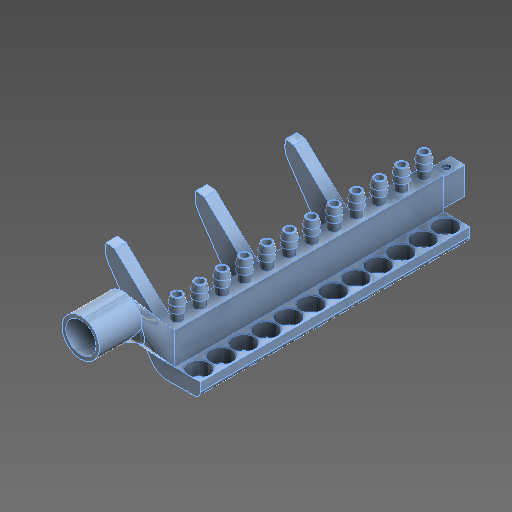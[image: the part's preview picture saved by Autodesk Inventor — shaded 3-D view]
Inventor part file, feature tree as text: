
AUTODESK INVENTOR PART (.ipt)
format: ipt  version: 2020 (Build 240168000, 168)  size: 707,584 bytes
history: native  units: in
note: dims shown in document units (in); Inventor stores cm internally (conversion verified against a paired STEP export)
features: other x13, extrude x7, pattern_linear x4, fillet x4, loft x2, projected_geometry x1, sketch x1
ambient origin geometry x8: Origin, YZ Plane, XZ Plane, XY Plane, X Axis, Y Axis, Z Axis, Center Point
bodies: Body1 (feature_tree)
feature tree (32):
  other  "CrossSection1"
  other  "Silicone Fitting Plane"
  other  "Cap Plane"
  other  "Base Sketch"
  extrude  "Base"  Depth=0.315in
  extrude  "Lip"  Depth=0.315in
  extrude  "Tube Socket"  Depth=0.315in
  pattern_linear  "Tube Socket Repetition"  Spacing1=0.0197in  [1 undecoded]
  other  "Silicone Fitting"
  pattern_linear  "Silicone Fitting Repetion"  Spacing1=0.5906in  [1 undecoded]
  extrude  "Coupling"  [1 undecoded]
  extrude  "Airflow Cut"  TaperAngle=0.0deg  [1 undecoded]
  pattern_linear  "Airflow Cut Repetition"  Spacing1=90.0deg  [1 undecoded]
  other  "Mouthpiece Adapter Plane"
  other  "Mouthpiece Adapter Loft To"
  loft  "Mouthpiece Adapter Outer"
  loft  "Moutpiece Adapter Inner"
  extrude  "Mouthpiece"  Depth=0.315in
  other  "Rule Fillet2"
  extrude  "Arm"  Depth=0.3214in
  fillet  "Fillet1"  [1 undecoded]
  fillet  "Fillet4"  Radius=0.7874in
  fillet  "Fillet6"  Radius=0.1607in
  pattern_linear  "Rectangular Pattern9"  Count1=3  [1 undecoded]
  fillet  "Fillet5"  [1 undecoded]
  other  "Silicone Fitting Sketch"
  other  "Airflow Cut Sketch"
  projected_geometry  "Projected Loop7"
  other  "Coupling Sketch"
  other  "Lip Sketch"
  sketch  "Sketch23"  dims[d87=0.0197in d88=0.0787in d89=-1.0625in d90=0.7874in d1=0.0591in d2=0.0591in d3=0.0591in d4=0.0197in d5=0.5906in d6=-0.2067in d8=0.0in d111=90.0deg d112=0.1181in d9=0.0in d12=-4.9606in d13=0.5906in d14=0.3214in d15=0.0in d122=0.7874in d124=0.1607in d125=1.1811in d128=0.0in d129=90.0deg d130=0.0in d131=90.0deg d132=0.0in d133=90.0deg d134=0.0in d135=90.0deg d136=0.7874in d137=0.0in d138=0.5512in d139=0.689in d140=0.7874in d141=0.0591in d142=0.0295in d143=0.0295in d144=0.0295in d145=0.0295in d146=0.0295in d147=0.0295in d148=0.0591in d155=5.1181in d157=0.4134in d158=4.7244in d160=0.4134in d161=4.9606in d163=0.3214in d164=0.0in d165=0.4724in d166=0.0in d167=0.3937in d168=0.2067in d169=0.2362in d170=0.3937in d171=0.0in d172=4.7244in d174=0.4134in d188=0.0157in d189=0.3214in d190=0.5906in d191=0.8661in d193=0.7874in d194=0.748in d197=0.1575in d200=0.2067in d201=0.0in d202=1.1811in d204=1.6535in d206=0.1181in d207=0.315in d209=0.315in d210=0.0481in]
  other  "Arm Sketch"
note: 8 required parameter values undecoded (feature->parameter linkage not recoverable at this tier; creation-order binding heuristic only, values carry confidence <= 0.55)
